# Revit family: CSBADA-36-3F-OCC11
name_source: partatom
category: Plumbing Fixtures
revit_build: Autodesk Revit MEP 2016 (Build: 20150220_1215(x64)
units: mm (PartAtom-declared; Revit-internal decimal feet)

## family parameters
Cut with Voids When Loaded = Yes
Host = Face
OmniClass Number = 23.45.05.14.17
OmniClass Title = Showers
Part Type = Normal
Room Calculation Point = No
Round Connector Dimension = Use Diameter
Shared = Yes

## types (1)
- CSBS-36-3F-OCC11
    AMA - Anti-Microbial Additive = No
    Assembly Code = D2010710
    CW Connection = Yes
    CWFU = 1.5
    Default Elevation = 0"
    Description = 36" ADA Corterra Shower Base, Square
    Finish = Corterra's-ACORN-Blanco
    HW Connection = Yes
    HWFU = 1.5
    Height = 6 3/8"
    Length = 37 1/8"
    Manufacturer = Acorn
    Model = CSBS-36-3F-OCC11
    OCC - Optional Corterra Color = No
    Product Documentation Link = https://www.acorneng.com
    Product URL = https://www.acorneng.com
    URL = http://www.acorneng.com
    Vent Connection = No
    WFU = 3
    Warranty Documentation Link = www.acorneng.com/terms-and-conditions
    Waste Connection = Yes
    Waste Connection Diameter = 2"
    Width = 38 3/8"

## geometry (parser evidence)
native form markers: Sweep x2
no freeform markers — native parametric forms only
